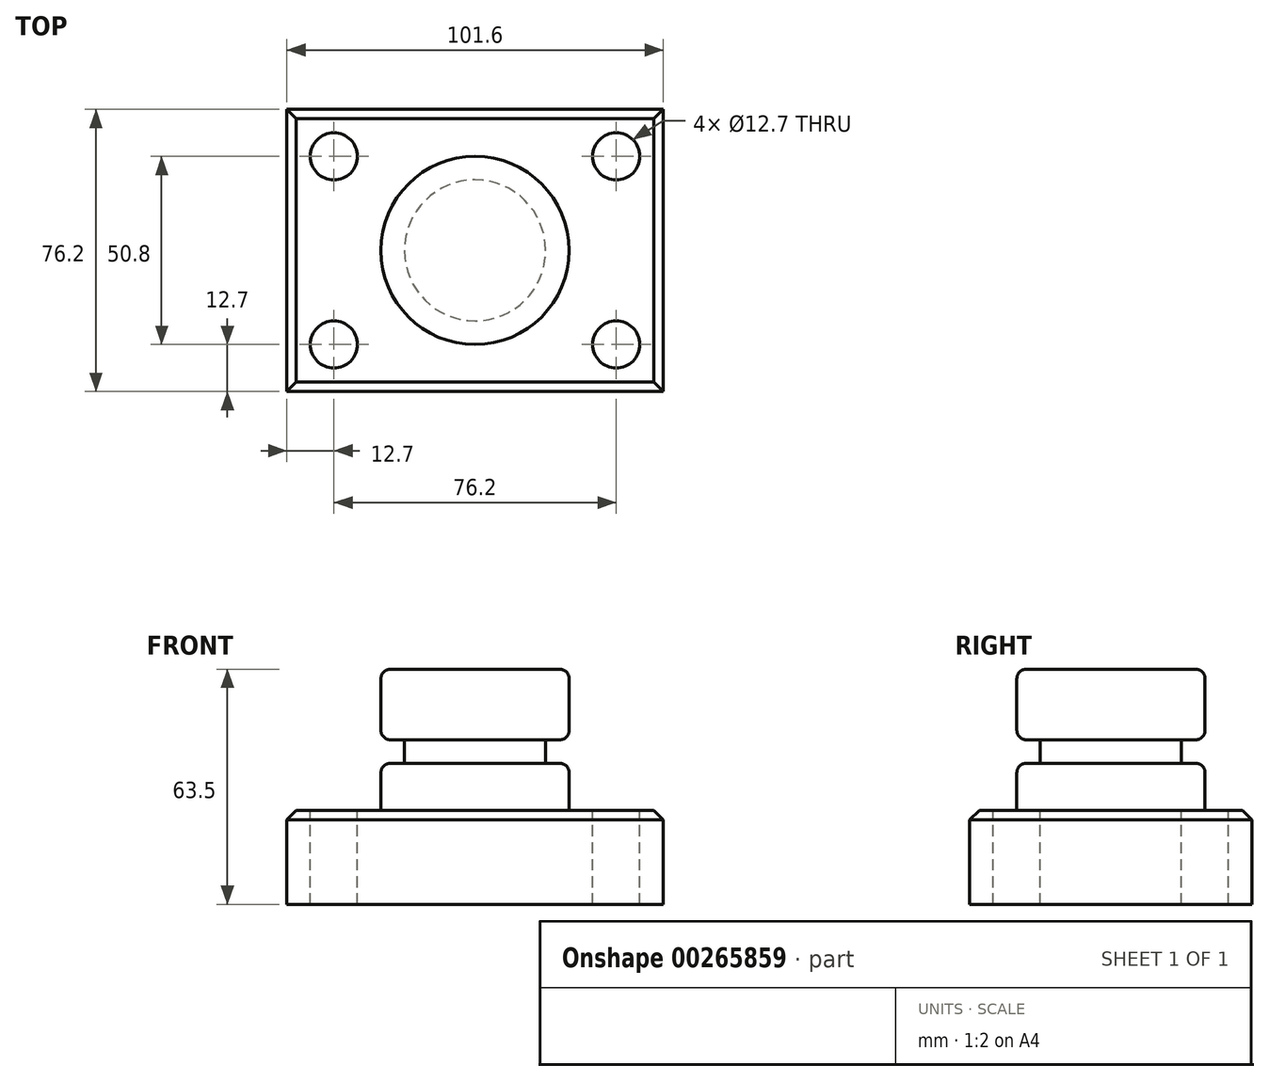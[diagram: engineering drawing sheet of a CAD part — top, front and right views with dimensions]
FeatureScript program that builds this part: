
annotation { "Feature Type Name" : "Feature", "Feature Type Description" : "" }
export const myFeature = defineFeature(function(context is Context, id is Id, definition is map)
    precondition{}
    {
        {
            var Q0;
            Q0=qCreatedBy(makeId("Top.planeOp"),FACE);
            var sketch = newSketch(context, id + "F0", { "sketchPlane" : qUnion([Q0])});
            skLineSegment(sketch, "E0.bottom", {"start": v(50.8, -38.1) * mm, "end": v(-50.8, -38.1) * mm});
            skLineSegment(sketch, "E0.top", {"start": v(50.8, 38.1) * mm, "end": v(-50.8, 38.1) * mm});
            skLineSegment(sketch, "E0.left", {"start": v(50.8, -38.1) * mm, "end": v(50.8, 38.1) * mm});
            skLineSegment(sketch, "E0.right", {"start": v(-50.8, -38.1) * mm, "end": v(-50.8, 38.1) * mm});
            skPoint(sketch, "E0.middle", {"position": v(0, 0) * mm});
            skSolve(sketch);
        }
        {
            var Q0;
            Q0=makeQuery(id+"F0.imprint","IMPRINT",FACE,{"disambiguationData":[TD([[makeQuery(id+"F0.imprint","IMPRINT",EDGE,{"derivedFrom":sQuery(id+"F0.wireOp",EDGE,"E0.bottom")}),-1.0]])]});
            extrude(context, id + "F1", {"entities" : qUnion([Q0]), "depth" : 25.4 * mm});
        }
        {
            var Q0;
            Q0=makeQuery(id+"F1.opExtrude","CAP_FACE",FACE,{"disambiguationData":[OSD([sQuery(id+"F0.wireOp",EDGE,"E0.bottom"),sQuery(id+"F0.wireOp",EDGE,"E0.top"),sQuery(id+"F0.wireOp",EDGE,"E0.left"),sQuery(id+"F0.wireOp",EDGE,"E0.right")])],"isStart":false});
            var sketch = newSketch(context, id + "F2", { "sketchPlane" : qUnion([Q0])});
            skCircle(sketch, "E1", {"center": v(-38.1, 25.4) * mm, "radius": 6.35 * mm});
            skCircle(sketch, "E2", {"center": v(38.1, 25.4) * mm, "radius": 6.35 * mm});
            skCircle(sketch, "E3", {"center": v(38.1, -25.4) * mm, "radius": 6.35 * mm});
            skCircle(sketch, "E4", {"center": v(-38.1, -25.4) * mm, "radius": 6.35 * mm});
            skSolve(sketch);
        }
        {
            var Q0;
            Q0 = qSketchRegion(id + "F2", true);
            extrude(context, id + "F3", {"entities" : qUnion([Q0]), "operationType" : NewBodyOperationType.REMOVE, "oppositeDirection" : true, "depth" : 25.4 * mm});
        }
        {
            var Q0;
            Q0=qCreatedBy(makeId("Front.planeOp"),FACE);
            var sketch = newSketch(context, id + "F4", { "sketchPlane" : qUnion([Q0])});
            skLineSegment(sketch, "E5.bottom", {"start": v(-25.4, 63.5) * mm, "end": v(0, 63.5) * mm});
            skLineSegment(sketch, "E5.top", {"start": v(-25.4, 25.4) * mm, "end": v(0, 25.4) * mm});
            skLineSegment(sketch, "E5.left", {"start": v(-25.4, 63.5) * mm, "end": v(-25.4, 25.4) * mm});
            skLineSegment(sketch, "E5.right", {"start": v(0, 63.5) * mm, "end": v(0, 25.4) * mm});
            skSolve(sketch);
        }
        {
            var Q0;
            Q0=makeQuery(id+"F4.imprint","IMPRINT",FACE,{"disambiguationData":[TD([[makeQuery(id+"F4.imprint","IMPRINT",EDGE,{"derivedFrom":sQuery(id+"F4.wireOp",EDGE,"E5.bottom")}),-1.0]])]});
            var Q1;
            Q1=sQuery(id+"F4.wireOp",EDGE,"E5.right");
            revolve(context, id + "F5", {"operationType" : NewBodyOperationType.ADD, "entities" : qUnion([Q0]), "axis" : qUnion([Q1]), "revolveType" : RevolveType.FULL});
        }
        {
            var Q0;
            Q0=qCreatedBy(makeId("Right.planeOp"),FACE);
            var sketch = newSketch(context, id + "F6", { "sketchPlane" : qUnion([Q0])});
            skLineSegment(sketch, "E6.bottom", {"start": v(-64.52, 44.45) * mm, "end": v(-19.05, 44.45) * mm});
            skLineSegment(sketch, "E6.top", {"start": v(-64.52, 38.1) * mm, "end": v(-19.05, 38.1) * mm});
            skLineSegment(sketch, "E6.left", {"start": v(-64.52, 44.45) * mm, "end": v(-64.52, 38.1) * mm});
            skLineSegment(sketch, "E6.right", {"start": v(-19.05, 44.45) * mm, "end": v(-19.05, 38.1) * mm});
            skSolve(sketch);
        }
        {
            var Q0;
            Q0=makeQuery(id+"F6.imprint","IMPRINT",FACE,{"disambiguationData":[TD([[makeQuery(id+"F6.imprint","IMPRINT",EDGE,{"derivedFrom":sQuery(id+"F6.wireOp",EDGE,"E6.bottom")}),-1.0]])]});
            var Q1;
            Q1=makeQuery(id+"F5.opRevolve","SWEPT_FACE",FACE,{"disambiguationData":[OSD([sQuery(id+"F4.wireOp",EDGE,"E5.left")])]});
            revolve(context, id + "F7", {"operationType" : NewBodyOperationType.REMOVE, "entities" : qUnion([Q0]), "axis" : qUnion([Q1]), "revolveType" : RevolveType.FULL, "oppositeDirection" : true});
        }
        {
            var Q0;
            Q0=makeQuery(id+"F1.opExtrude","CAP_EDGE",EDGE,{"disambiguationData":[OSD([sQuery(id+"F0.wireOp",EDGE,"E0.left")])],"isStart":false});
            var Q1;
            Q1=makeQuery(id+"F1.opExtrude","CAP_EDGE",EDGE,{"disambiguationData":[OSD([sQuery(id+"F0.wireOp",EDGE,"E0.top")])],"isStart":false});
            var Q2;
            Q2=makeQuery(id+"F1.opExtrude","CAP_EDGE",EDGE,{"disambiguationData":[OSD([sQuery(id+"F0.wireOp",EDGE,"E0.right")])],"isStart":false});
            var Q3;
            Q3=makeQuery(id+"F1.opExtrude","CAP_EDGE",EDGE,{"disambiguationData":[OSD([sQuery(id+"F0.wireOp",EDGE,"E0.bottom")])],"isStart":false});
            chamfer(context, id + "F8", {"entities" : qUnion([Q0, Q1, Q2, Q3]), "width" : 2.54 * mm, "tangentPropagation" : true});
        }
        {
            var Q0;
            Q0=makeQuery(id+"F7.boolean.opBoolean","INTERSECT",EDGE,{"derivedFrom":[makeQuery(id+"F5.opRevolve","SWEPT_FACE",FACE,{"disambiguationData":[OSD([sQuery(id+"F4.wireOp",EDGE,"E5.left")])]}),makeQuery(id+"F7.opRevolve","SWEPT_FACE",FACE,{"disambiguationData":[OSD([sQuery(id+"F6.wireOp",EDGE,"E6.bottom")])]})]});
            var Q1;
            Q1=makeQuery(id+"F7.boolean.opBoolean","INTERSECT",EDGE,{"derivedFrom":[makeQuery(id+"F5.opRevolve","SWEPT_FACE",FACE,{"disambiguationData":[OSD([sQuery(id+"F4.wireOp",EDGE,"E5.left")])]}),makeQuery(id+"F7.opRevolve","SWEPT_FACE",FACE,{"disambiguationData":[OSD([sQuery(id+"F6.wireOp",EDGE,"E6.top")])]})]});
            var Q2;
            Q2=makeQuery(id+"F5.opRevolve","SWEPT_EDGE",EDGE,{"disambiguationData":[OSD([sQuery(id+"F4.wireOp",EDGE,"E5.bottom"),sQuery(id+"F4.wireOp",EDGE,"E5.left")])]});
            var Q3;
            Q3=makeQuery(id+"F5.opRevolve","SWEPT_EDGE",EDGE,{"disambiguationData":[OSD([sQuery(id+"F4.wireOp",EDGE,"E5.top"),sQuery(id+"F4.wireOp",EDGE,"E5.left")])]});
            fillet(context, id + "F9", {"entities" : qUnion([Q0, Q1, Q2, Q3]), "radius" : 2.54 * mm, "tangentPropagation" : true, "allowEdgeOverflow" : false});
        }
    });
